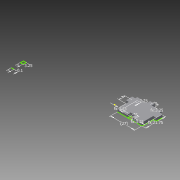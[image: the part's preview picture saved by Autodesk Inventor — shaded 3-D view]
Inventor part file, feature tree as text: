
AUTODESK INVENTOR PART (.ipt)
format: ipt  version: 2013 (Build 170138000, 138)  size: 118,272 bytes
history: native  units: mm
features: extrude x4, other x2, sketch x1
ambient origin geometry x8: Origin, YZ Plane, XZ Plane, XY Plane, X Axis, Y Axis, Z Axis, Center Point
feature tree (7):
  other  "Blocks"
  sketch  "Sketch1"  dims[d0=3.0mm d2=3.0mm d3=0.1mm d7=22.5mm d8=12.4mm d9=4.5mm d10=4.5mm d11=2.0mm d12=2.0mm d58=27.0mm d59=21.75mm d60=5.0mm d61=3.25mm d62=3.25mm d63=0.0mm d64=3.25mm d65=7.0mm d66=5.0mm d67=3.25mm d68=3.25mm d69=0.0mm d70=2.25mm d71=3.25mm d72=0.0mm d73=3.25mm d74=0.0mm d75=27.0mm]
  extrude  "Extrusion5"  Depth=3.0mm
  extrude  "Extrusion6"  Depth=27.0mm
  extrude  "Extrusion7"  Depth=21.75mm
  extrude  "Extrusion8"  Depth=5.0mm
  other  "Block1"
